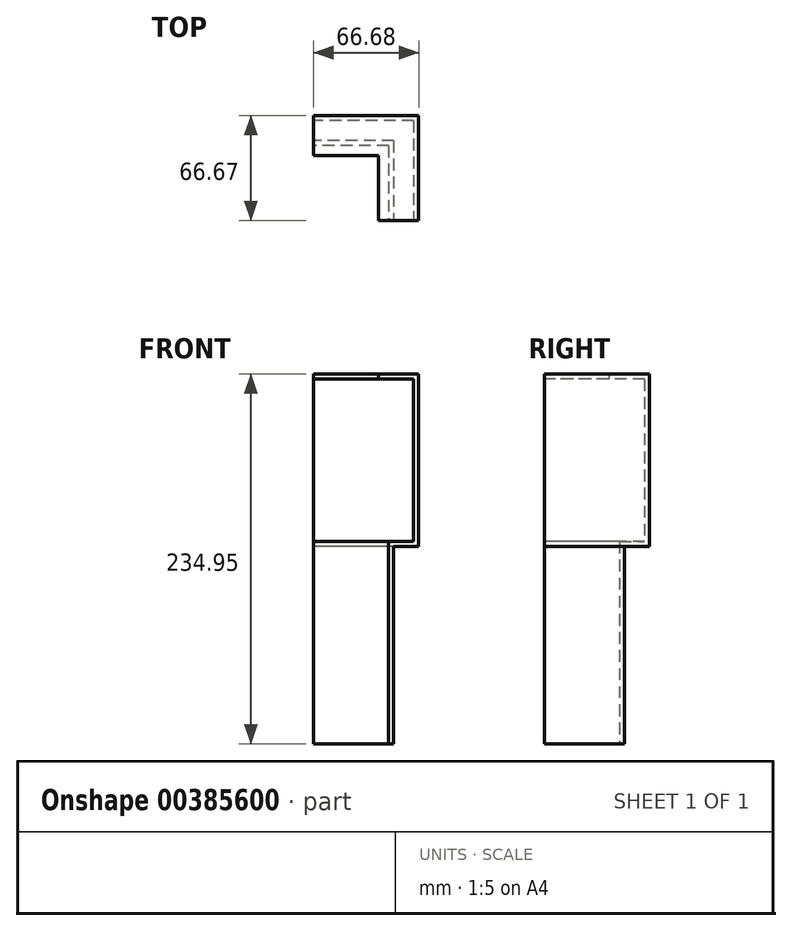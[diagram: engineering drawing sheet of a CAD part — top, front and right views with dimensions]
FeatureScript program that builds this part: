
annotation { "Feature Type Name" : "Feature", "Feature Type Description" : "" }
export const myFeature = defineFeature(function(context is Context, id is Id, definition is map)
    precondition{}
    {
        {
            var Q0;
            Q0=qCreatedBy(makeId("Right.planeOp"),FACE);
            var sketch = newSketch(context, id + "F0", { "sketchPlane" : qUnion([Q0])});
            skLineSegment(sketch, "E0", {"start": v(0, 0) * mm, "end": v(0, 128.59) * mm});
            skLineSegment(sketch, "E1", {"start": v(0, 128.59) * mm, "end": v(15.87, 128.59) * mm});
            skLineSegment(sketch, "E2", {"start": v(15.87, 128.59) * mm, "end": v(15.87, 231.78) * mm});
            skLineSegment(sketch, "E3", {"start": v(15.87, 231.78) * mm, "end": v(-6.35, 231.78) * mm});
            skLineSegment(sketch, "E4", {"start": v(-6.35, 231.78) * mm, "end": v(-6.35, 234.95) * mm});
            skLineSegment(sketch, "E5", {"start": v(-6.35, 234.95) * mm, "end": v(19.05, 234.95) * mm});
            skLineSegment(sketch, "E6", {"start": v(19.05, 234.95) * mm, "end": v(19.05, 125.41) * mm});
            skLineSegment(sketch, "E7", {"start": v(19.05, 125.41) * mm, "end": v(3.17, 125.41) * mm});
            skLineSegment(sketch, "E8", {"start": v(3.17, 125.41) * mm, "end": v(3.18, 0) * mm});
            skLineSegment(sketch, "E9", {"start": v(3.18, 0) * mm, "end": v(0, 0) * mm});
            skSolve(sketch);
        }
        {
            var Q0;
            Q0=makeQuery(id+"F0.imprint","IMPRINT",FACE,{"disambiguationData":[TD([[makeQuery(id+"F0.imprint","IMPRINT",EDGE,{"derivedFrom":sQuery(id+"F0.wireOp",EDGE,"E0")}),-1.0]])]});
            extrude(context, id + "F1", {"entities" : qUnion([Q0]), "depth" : 66.67 * mm});
        }
        {
            var Q0;
            Q0=makeQuery(id+"F1.opExtrude","SWEPT_FACE",FACE,{"disambiguationData":[OSD([sQuery(id+"F0.wireOp",EDGE,"E5")])]});
            var sketch = newSketch(context, id + "F2", { "sketchPlane" : qUnion([Q0])});
            skLineSegment(sketch, "E10", {"start": v(66.68, 19.05) * mm, "end": v(41.28, -6.35) * mm});
            skLineSegment(sketch, "E11", {"start": v(66.68, 19.05) * mm, "end": v(66.68, -6.35) * mm});
            skLineSegment(sketch, "E12", {"start": v(66.68, -6.35) * mm, "end": v(41.28, -6.35) * mm});
            skSolve(sketch);
        }
        {
            var Q0;
            Q0=makeQuery(id+"F2.imprint","IMPRINT",FACE,{"disambiguationData":[TD([[makeQuery(id+"F2.imprint","IMPRINT",EDGE,{"derivedFrom":sQuery(id+"F2.wireOp",EDGE,"E10")}),1.0]])]});
            extrude(context, id + "F3", {"entities" : qUnion([Q0]), "operationType" : NewBodyOperationType.REMOVE, "endBound" : BoundingType.THROUGH_ALL, "oppositeDirection" : true, "depth" : 25.4 * mm});
        }
        {
            var Q0;
            Q0=makeQuery(id+"F1.opExtrude","SWEPT_BODY",BODY,{"disambiguationData":[OSD([sQuery(id+"F0.wireOp",EDGE,"E0"),sQuery(id+"F0.wireOp",EDGE,"E1"),sQuery(id+"F0.wireOp",EDGE,"E2"),sQuery(id+"F0.wireOp",EDGE,"E3"),sQuery(id+"F0.wireOp",EDGE,"E4"),sQuery(id+"F0.wireOp",EDGE,"E5"),sQuery(id+"F0.wireOp",EDGE,"E6"),sQuery(id+"F0.wireOp",EDGE,"E7"),sQuery(id+"F0.wireOp",EDGE,"E8"),sQuery(id+"F0.wireOp",EDGE,"E9")])]});
            var Q1;
            Q1=makeQuery(id+"F3.boolean.opBoolean","COPY",FACE,{"derivedFrom":makeQuery(id+"F3.opExtrude","SWEPT_FACE",FACE,{"disambiguationData":[OSD([sQuery(id+"F2.wireOp",EDGE,"E10")])]})});
            mirror(context, id + "F4", {"operationType" : NewBodyOperationType.ADD, "entities" : qUnion([Q0]), "mirrorPlane" : qUnion([Q1])});
        }
    });
